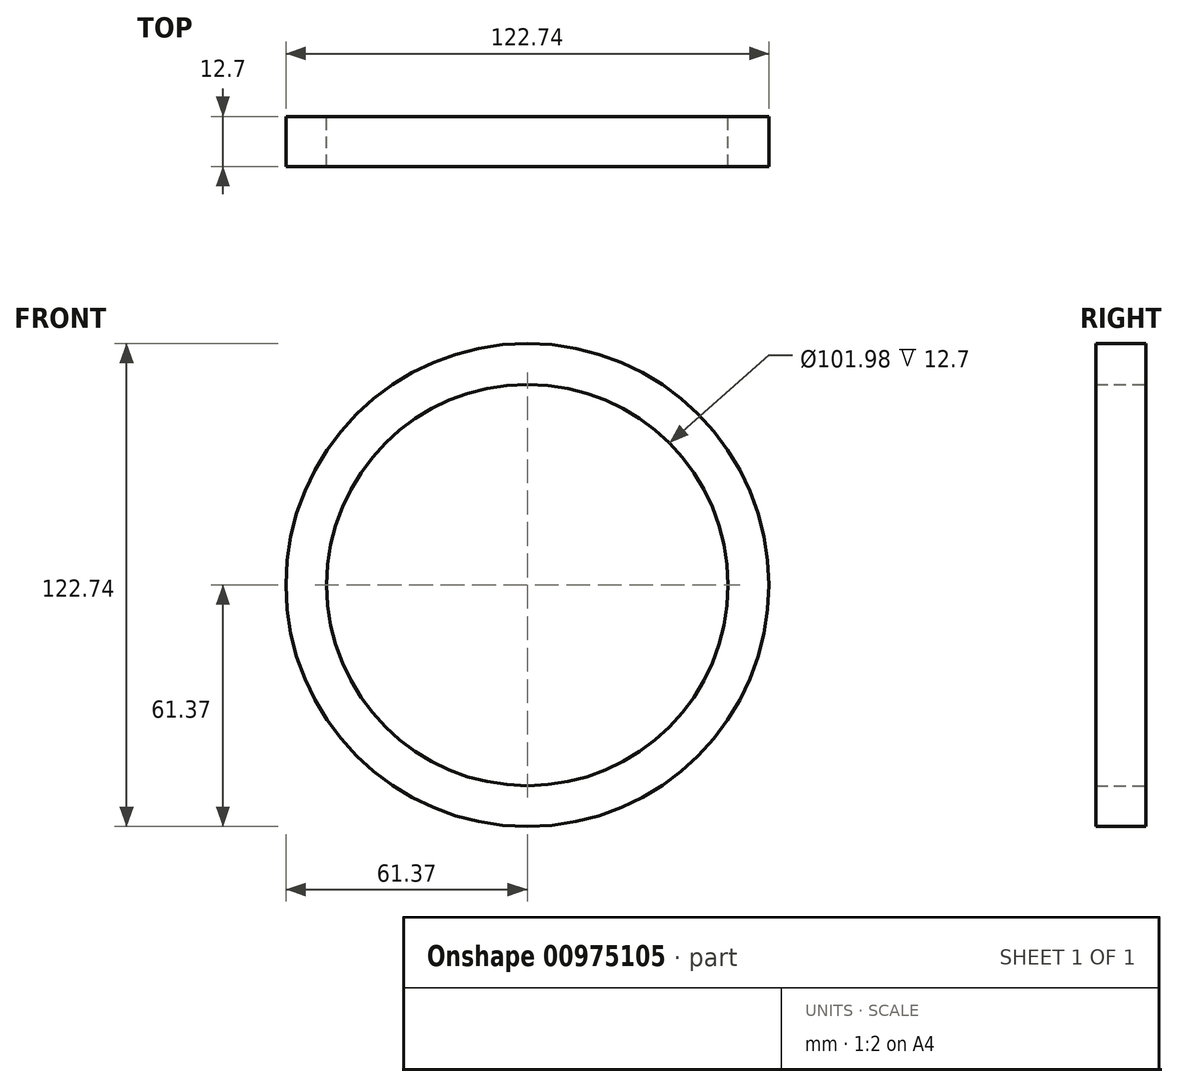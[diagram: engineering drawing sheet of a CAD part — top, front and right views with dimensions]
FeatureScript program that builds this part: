
annotation { "Feature Type Name" : "Feature", "Feature Type Description" : "" }
export const myFeature = defineFeature(function(context is Context, id is Id, definition is map)
    precondition{}
    {
        {
            var Q0;
            Q0=qCreatedBy(makeId("Front.planeOp"),FACE);
            var sketch = newSketch(context, id + "F0", { "sketchPlane" : qUnion([Q0])});
            skCircle(sketch, "E0", {"center": v(0, 0) * mm, "radius": 51 * mm});
            skCircle(sketch, "E1", {"center": v(0, 0) * mm, "radius": 61.37 * mm});
            skSolve(sketch);
        }
        {
            var Q0;
            Q0 = qSketchRegion(id + "F0", true);
            extrude(context, id + "F1", {"entities" : qUnion([Q0]), "flatOperationType" : FlatOperationType.REMOVE, "depth" : 12.7 * mm, "offsetDistance" : 25.4 * mm, "domain" : OperationDomain.MODEL});
        }
    });
